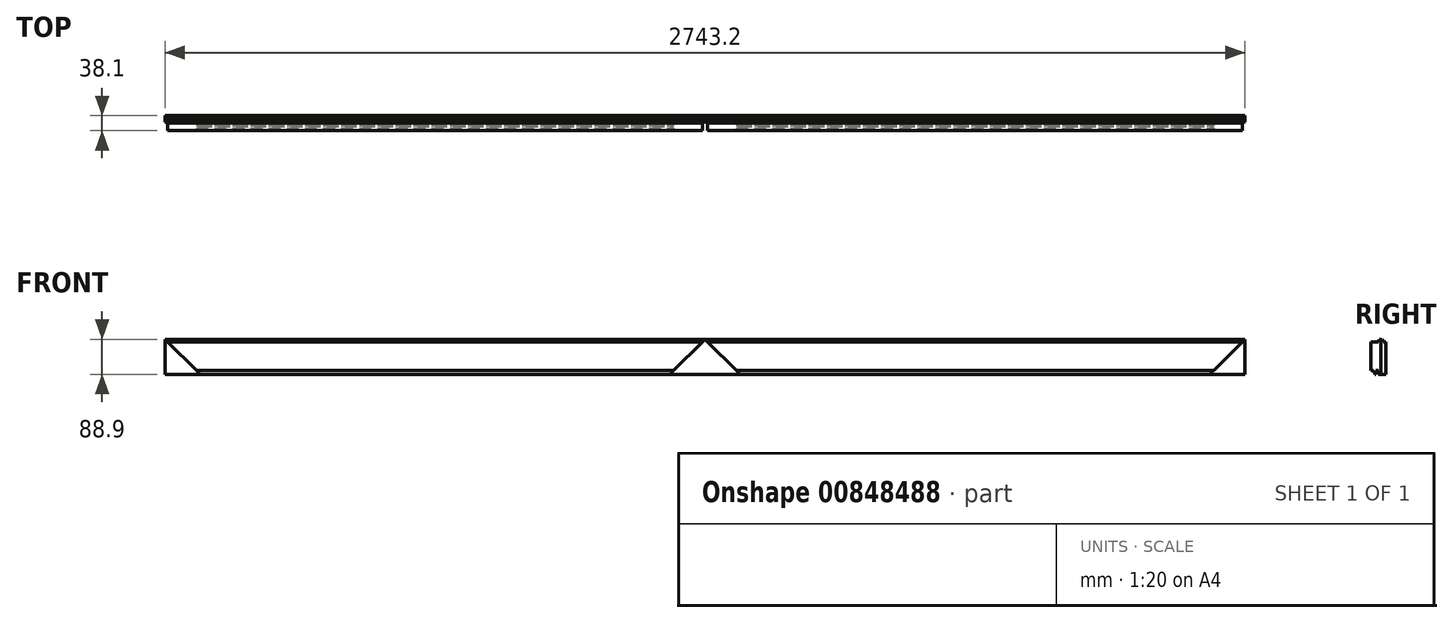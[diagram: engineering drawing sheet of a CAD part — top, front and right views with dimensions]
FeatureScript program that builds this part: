
annotation { "Feature Type Name" : "Feature", "Feature Type Description" : "" }
export const myFeature = defineFeature(function(context is Context, id is Id, definition is map)
    precondition{}
    {
        {
            var Q0;
            Q0=qCreatedBy(makeId("Front.planeOp"),FACE);
            var sketch = newSketch(context, id + "F0", { "sketchPlane" : qUnion([Q0])});
            skLineSegment(sketch, "E0.bottom", {"start": v(-1371.6, 44.45) * mm, "end": v(1371.6, 44.45) * mm});
            skLineSegment(sketch, "E0.top", {"start": v(-1371.6, -44.45) * mm, "end": v(1371.6, -44.45) * mm});
            skLineSegment(sketch, "E0.left", {"start": v(-1371.6, 44.45) * mm, "end": v(-1371.6, -44.45) * mm});
            skLineSegment(sketch, "E0.right", {"start": v(1371.6, 44.45) * mm, "end": v(1371.6, -44.45) * mm});
            skPoint(sketch, "E0.middle", {"position": v(0, 0) * mm});
            skSolve(sketch);
        }
        {
            var Q0;
            Q0=qSketchRegion(id+"F0",true);
            extrude(context, id + "F1", {"entities" : qUnion([Q0]), "oppositeDirection" : true, "depth" : 38.1 * mm, "offsetDistance" : 25.4 * mm});
        }
        {
            var Q0;
            Q0=makeQuery(id+"F1.opExtrude","SWEPT_FACE",FACE,{"disambiguationData":[OSD([sQuery(id+"F0.wireOp",EDGE,"E0.right")])]});
            var sketch = newSketch(context, id + "F2", { "sketchPlane" : qUnion([Q0])});
            skLineSegment(sketch, "E1", {"start": v(38.1, 44.45) * mm, "end": v(38.1, 38.1) * mm});
            skLineSegment(sketch, "E2", {"start": v(38.1, 38.1) * mm, "end": v(31.75, 38.1) * mm});
            skLineSegment(sketch, "E3", {"start": v(31.75, 38.1) * mm, "end": v(28.58, 44.45) * mm});
            skLineSegment(sketch, "E4", {"start": v(22.23, 44.45) * mm, "end": v(19.05, 38.1) * mm});
            skLineSegment(sketch, "E5", {"start": v(19.05, 38.1) * mm, "end": v(0, 38.1) * mm});
            skLineSegment(sketch, "E6", {"start": v(0, 38.1) * mm, "end": v(0, 44.45) * mm});
            skLineSegment(sketch, "E7", {"start": v(0, 44.45) * mm, "end": v(22.22, 44.45) * mm});
            skLineSegment(sketch, "E8", {"start": v(28.58, 44.45) * mm, "end": v(38.1, 44.45) * mm});
            skSolve(sketch);
        }
        {
            var Q0;
            Q0=qSketchRegion(id+"F2",true);
            extrude(context, id + "F3", {"entities" : qUnion([Q0]), "operationType" : NewBodyOperationType.REMOVE, "endBound" : BoundingType.THROUGH_ALL, "oppositeDirection" : true, "depth" : 25.4 * mm, "offsetDistance" : 25.4 * mm});
        }
        {
            var Q0;
            Q0=makeQuery(id+"F1.opExtrude","SWEPT_FACE",FACE,{"disambiguationData":[OSD([sQuery(id+"F0.wireOp",EDGE,"E0.right")])]});
            var sketch = newSketch(context, id + "F4", { "sketchPlane" : qUnion([Q0])});
            skLineSegment(sketch, "E9", {"start": v(0, -34.92) * mm, "end": v(6.35, -34.92) * mm});
            skLineSegment(sketch, "E10", {"start": v(12.7, -34.92) * mm, "end": v(19.05, -34.92) * mm});
            skLineSegment(sketch, "E11", {"start": v(12.7, -34.92) * mm, "end": v(12.7, -44.45) * mm});
            skLineSegment(sketch, "E12", {"start": v(19.05, -44.45) * mm, "end": v(19.05, -34.92) * mm});
            skLineSegment(sketch, "E13", {"start": v(10.65, -44.45) * mm, "end": v(0, -44.45) * mm});
            skLineSegment(sketch, "E14", {"start": v(0, -34.92) * mm, "end": v(0, -44.45) * mm});
            skLineSegment(sketch, "E15", {"start": v(12.7, -44.45) * mm, "end": v(19.05, -44.45) * mm});
            skArc(sketch, "E16", {"start": v(6.35, -34.92) * mm, "mid": v(6.91, -37.54) * mm, "end": v(8.5, -39.69) * mm});
            skArc(sketch, "E17", {"start": v(10.65, -44.45) * mm, "mid": v(10.09, -41.84) * mm, "end": v(8.5, -39.69) * mm});
            skSolve(sketch);
        }
        {
            var Q0;
            Q0=qSketchRegion(id+"F4",true);
            extrude(context, id + "F5", {"entities" : qUnion([Q0]), "operationType" : NewBodyOperationType.REMOVE, "endBound" : BoundingType.THROUGH_ALL, "oppositeDirection" : true, "depth" : 25.4 * mm, "offsetDistance" : 25.4 * mm});
        }
        {
            var Q0;
            Q0=makeQuery(id+"F1.opExtrude","CAP_FACE",FACE,{"disambiguationData":[OSD([sQuery(id+"F0.wireOp",EDGE,"E0.bottom"),sQuery(id+"F0.wireOp",EDGE,"E0.top"),sQuery(id+"F0.wireOp",EDGE,"E0.left"),sQuery(id+"F0.wireOp",EDGE,"E0.right")])],"isStart":true});
            var sketch = newSketch(context, id + "F6", { "sketchPlane" : qUnion([Q0])});
            skLineSegment(sketch, "E18", {"start": v(-1282.7, -44.45) * mm, "end": v(-1371.6, 44.45) * mm});
            skLineSegment(sketch, "E19", {"start": v(-1282.7, -44.45) * mm, "end": v(-1371.6, -44.45) * mm});
            skLineSegment(sketch, "E20", {"start": v(-1371.6, 44.45) * mm, "end": v(-1371.6, -44.45) * mm});
            skLineSegment(sketch, "E21", {"start": v(0, 760.27) * mm, "end": v(0, -577.9) * mm, "construction": true});
            skLineSegment(sketch, "E22", {"start": v(-89, -44.45) * mm, "end": v(0, 44.55) * mm});
            skLineSegment(sketch, "E23", {"start": v(-89, -44.45) * mm, "end": v(0, -44.45) * mm});
            skLineSegment(sketch, "E24.MirrorCS", {"start": v(89, -44.45) * mm, "end": v(0, -44.45) * mm});
            skLineSegment(sketch, "E25.MirrorCS", {"start": v(89, -44.45) * mm, "end": v(0, 44.55) * mm});
            skLineSegment(sketch, "E26.MirrorCS", {"start": v(1371.6, 44.45) * mm, "end": v(1371.6, -44.45) * mm});
            skLineSegment(sketch, "E27.MirrorCS", {"start": v(1282.7, -44.45) * mm, "end": v(1371.6, 44.45) * mm});
            skLineSegment(sketch, "E28.MirrorCS", {"start": v(1282.7, -44.45) * mm, "end": v(1371.6, -44.45) * mm});
            skSolve(sketch);
        }
        {
            var Q0;
            Q0=qSketchRegion(id+"F6",true);
            extrude(context, id + "F7", {"entities" : qUnion([Q0]), "operationType" : NewBodyOperationType.REMOVE, "oppositeDirection" : true, "depth" : 25.4 * mm, "offsetDistance" : 25.4 * mm});
        }
    });
